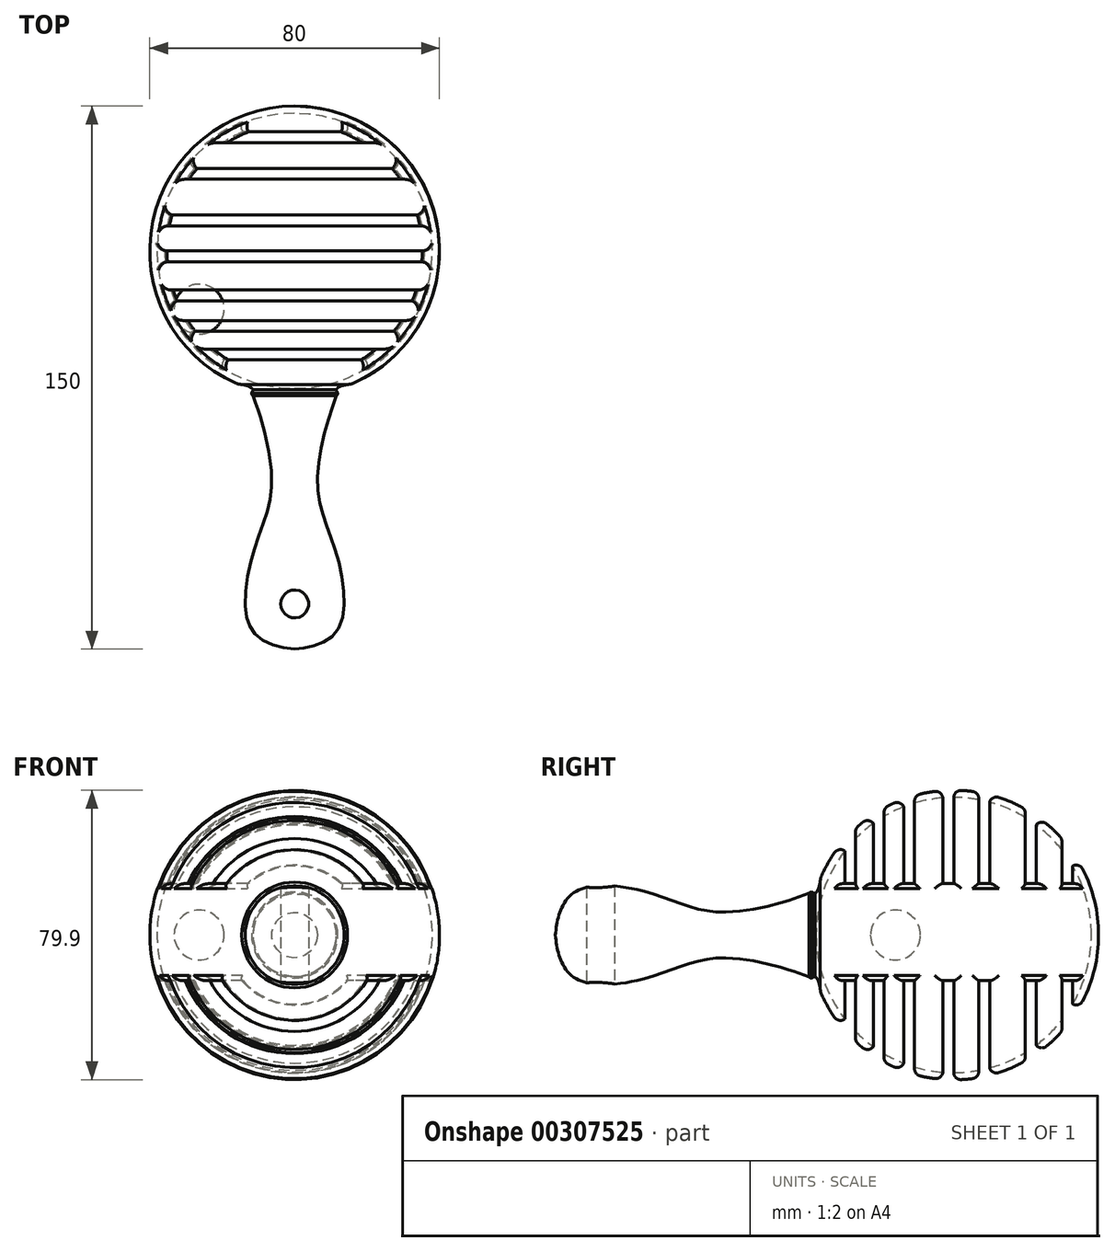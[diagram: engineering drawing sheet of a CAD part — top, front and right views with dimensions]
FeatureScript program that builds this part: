
annotation { "Feature Type Name" : "Feature", "Feature Type Description" : "" }
export const myFeature = defineFeature(function(context is Context, id is Id, definition is map)
    precondition{}
    {
        {
            var Q0;
            Q0=qCreatedBy(makeId("Top.planeOp"),FACE);
            var sketch = newSketch(context, id + "F0", { "sketchPlane" : qUnion([Q0])});
            skArc(sketch, "E0", {"start": v(11.53, -38.3) * mm, "mid": v(39.57, 5.83) * mm, "end": v(0, 40) * mm});
            skArc(sketch, "E1", {"start": v(0, -38) * mm, "mid": v(38, 0) * mm, "end": v(0, 38) * mm});
            skLineSegment(sketch, "E2", {"start": v(0, 40) * mm, "end": v(0, 38) * mm});
            skPoint(sketch, "E3.orphan", {"position": v(0, 47.99) * mm});
            skLineSegment(sketch, "E4.trimOffspring", {"start": v(0, -38) * mm, "end": v(0, -40) * mm});
            skLineSegment(sketch, "E5.bottom", {"start": v(0, -40) * mm, "end": v(11.53, -40) * mm, "construction": true});
            skLineSegment(sketch, "E5.top", {"start": v(0, -110) * mm, "end": v(11.53, -110) * mm, "construction": true});
            skLineSegment(sketch, "E5.left", {"start": v(0, -40) * mm, "end": v(0, -110) * mm, "construction": true});
            skLineSegment(sketch, "E5.right", {"start": v(11.53, -40) * mm, "end": v(11.53, -110) * mm, "construction": true});
            skFitSpline(sketch, "E6", {"points": [v(11.53, -40) * mm, v(6.31, -64.44) * mm, v(11.53, -83.61) * mm, v(11.53, -105.15) * mm, v(0, -110) * mm], "startDerivative": vector(-24.57, -62.37) * mm, "endDerivative": vector(-51.62, -4) * mm});
            skLineSegment(sketch, "E7", {"start": v(0, -110) * mm, "end": v(0, -38) * mm});
            skFitSpline(sketch, "E8", {"points": [v(11.53, -40) * mm, v(11.53, -38.3) * mm, v(15.84, -36.73) * mm, v(13.87, -37.35) * mm], "startDerivative": vector(9.54, 10.18) * mm, "endDerivative": vector(-21.06, -2.87) * mm});
            skFitSpline(sketch, "E9", {"points": [v(11.53, -40) * mm, v(11.53, -38.3) * mm, v(15.3, -37.1) * mm, v(14.9, -38.3) * mm], "startDerivative": vector(8.59, 7.83) * mm, "endDerivative": vector(-7.06, -1.53) * mm});
            skSolve(sketch);
        }
        {
            var Q0;
            {var subQ1=sQuery(id+"F0.wireOp",EDGE,"E1");Q0=makeQuery(id+"F0.imprint","IMPRINT",FACE,{"disambiguationData":[TD([[makeQuery(id+"F0.imprint","IMPRINT",EDGE,{"derivedFrom":subQ1}),-1.0]])]});}
            var Q1;
            Q1=sQuery(id+"F0.wireOp",EDGE,"E7");
            revolve(context, id + "F1", {"entities" : qUnion([Q0]), "axis" : qUnion([Q1]), "revolveType" : RevolveType.FULL});
        }
        {
            var Q0;
            Q0=qCreatedBy(makeId("Right.planeOp"),FACE);
            var sketch = newSketch(context, id + "F2", { "sketchPlane" : qUnion([Q0])});
            skLineSegment(sketch, "E10.bottom", {"start": v(-30.1, 14.18) * mm, "end": v(-27.1, 14.18) * mm});
            skLineSegment(sketch, "E11.bottom", {"start": v(-30.1, 48.04) * mm, "end": v(-27.1, 48.04) * mm});
            skLineSegment(sketch, "E11.top", {"start": v(-30.1, -43.05) * mm, "end": v(-27.1, -43.05) * mm});
            skLineSegment(sketch, "E11.left", {"start": v(-30.1, 48.04) * mm, "end": v(-30.1, 14.18) * mm});
            skLineSegment(sketch, "E11.right", {"start": v(-27.1, 48.04) * mm, "end": v(-27.1, 14.18) * mm});
            skLineSegment(sketch, "E12.bottom", {"start": v(-22.22, 48.3) * mm, "end": v(-19.22, 48.3) * mm});
            skLineSegment(sketch, "E12.top", {"start": v(-22.22, -43.31) * mm, "end": v(-19.22, -43.31) * mm});
            skLineSegment(sketch, "E12.left", {"start": v(-22.22, 48.3) * mm, "end": v(-22.22, 14.18) * mm});
            skLineSegment(sketch, "E12.right", {"start": v(-19.22, 48.3) * mm, "end": v(-19.22, 14.18) * mm});
            skLineSegment(sketch, "E13.bottom", {"start": v(-13.82, 48.04) * mm, "end": v(-10.82, 48.04) * mm});
            skLineSegment(sketch, "E13.top", {"start": v(-13.82, -46.73) * mm, "end": v(-10.82, -46.73) * mm});
            skLineSegment(sketch, "E13.left", {"start": v(-13.82, 48.04) * mm, "end": v(-13.82, 14.18) * mm});
            skLineSegment(sketch, "E13.right", {"start": v(-10.82, 48.04) * mm, "end": v(-10.82, 14.18) * mm});
            skLineSegment(sketch, "E14.bottom", {"start": v(-3, 49.61) * mm, "end": v(0, 49.61) * mm});
            skLineSegment(sketch, "E14.top", {"start": v(-3, -50.66) * mm, "end": v(0, -50.66) * mm});
            skLineSegment(sketch, "E14.left", {"start": v(-3, 49.61) * mm, "end": v(-3, 14.18) * mm});
            skLineSegment(sketch, "E14.right", {"start": v(0, 49.61) * mm, "end": v(0, 14.18) * mm});
            skPoint(sketch, "E15.firstSnap0", {"position": v(6.92, 14.18) * mm});
            skLineSegment(sketch, "E15.bottom", {"start": v(6.92, 48.83) * mm, "end": v(9.92, 48.83) * mm});
            skLineSegment(sketch, "E15.top", {"start": v(6.92, -54.34) * mm, "end": v(9.92, -54.34) * mm});
            skLineSegment(sketch, "E15.left", {"start": v(6.92, 48.83) * mm, "end": v(6.92, 14.18) * mm});
            skLineSegment(sketch, "E15.right", {"start": v(9.92, 48.83) * mm, "end": v(9.92, 14.18) * mm});
            skLineSegment(sketch, "E16.bottom", {"start": v(19.78, 48.83) * mm, "end": v(22.78, 48.83) * mm});
            skLineSegment(sketch, "E16.top", {"start": v(19.78, -47.78) * mm, "end": v(22.78, -47.78) * mm});
            skLineSegment(sketch, "E16.left", {"start": v(19.78, 48.83) * mm, "end": v(19.78, 14.18) * mm});
            skLineSegment(sketch, "E16.right", {"start": v(22.78, 48.83) * mm, "end": v(22.78, 14.18) * mm});
            skLineSegment(sketch, "E17.bottom", {"start": v(29.87, 48.3) * mm, "end": v(32.87, 48.3) * mm});
            skLineSegment(sketch, "E17.top", {"start": v(29.87, -47.78) * mm, "end": v(32.87, -47.78) * mm});
            skLineSegment(sketch, "E17.left", {"start": v(29.87, 48.3) * mm, "end": v(29.87, 14.18) * mm});
            skLineSegment(sketch, "E17.right", {"start": v(32.87, 48.3) * mm, "end": v(32.87, 14.18) * mm});
            skPoint(sketch, "E18.orphan", {"position": v(46.3, 14.18) * mm});
            skLineSegment(sketch, "E19.trimOffspring", {"start": v(29.87, 14.18) * mm, "end": v(32.87, 14.18) * mm});
            skLineSegment(sketch, "E20.trimOffspring", {"start": v(29.87, -12.6) * mm, "end": v(29.87, -47.78) * mm});
            skLineSegment(sketch, "E21.trimOffspring", {"start": v(32.87, -12.6) * mm, "end": v(32.87, -47.78) * mm});
            skLineSegment(sketch, "E22.trimOffspring", {"start": v(22.78, -12.6) * mm, "end": v(22.78, -47.78) * mm});
            skLineSegment(sketch, "E23.trimOffspring", {"start": v(19.78, -12.6) * mm, "end": v(19.78, -47.78) * mm});
            skLineSegment(sketch, "E24.trimOffspring", {"start": v(9.92, -12.6) * mm, "end": v(9.92, -54.34) * mm});
            skLineSegment(sketch, "E25.trimOffspring", {"start": v(6.92, -12.6) * mm, "end": v(6.92, -54.34) * mm});
            skLineSegment(sketch, "E26.trimOffspring", {"start": v(0, -12.6) * mm, "end": v(0, -50.66) * mm});
            skLineSegment(sketch, "E27.trimOffspring", {"start": v(-3, -12.6) * mm, "end": v(-3, -50.66) * mm});
            skLineSegment(sketch, "E28.trimOffspring", {"start": v(-10.82, -12.6) * mm, "end": v(-10.82, -46.73) * mm});
            skLineSegment(sketch, "E29.trimOffspring", {"start": v(-13.82, -12.6) * mm, "end": v(-13.82, -46.73) * mm});
            skLineSegment(sketch, "E30.trimOffspring", {"start": v(-19.22, -12.6) * mm, "end": v(-19.22, -43.31) * mm});
            skLineSegment(sketch, "E31.trimOffspring", {"start": v(-22.22, -12.6) * mm, "end": v(-22.22, -43.31) * mm});
            skLineSegment(sketch, "E32.trimOffspring", {"start": v(-27.1, -12.6) * mm, "end": v(-27.1, -43.05) * mm});
            skLineSegment(sketch, "E33.trimOffspring", {"start": v(-30.1, -12.6) * mm, "end": v(-30.1, -43.05) * mm});
            skLineSegment(sketch, "E34.trimOffspring", {"start": v(-22.22, 14.18) * mm, "end": v(-19.22, 14.18) * mm});
            skPoint(sketch, "E35.orphan", {"position": v(-32.46, 14.18) * mm});
            skLineSegment(sketch, "E36.trimOffspring", {"start": v(-13.82, 14.18) * mm, "end": v(-10.82, 14.18) * mm});
            skLineSegment(sketch, "E37", {"start": v(-3, 14.18) * mm, "end": v(0, 14.18) * mm});
            skLineSegment(sketch, "E38", {"start": v(6.92, 14.18) * mm, "end": v(9.92, 14.18) * mm});
            skLineSegment(sketch, "E39", {"start": v(19.78, 14.18) * mm, "end": v(22.78, 14.18) * mm});
            skLineSegment(sketch, "E40", {"start": v(-30.1, -12.6) * mm, "end": v(-27.1, -12.6) * mm});
            skLineSegment(sketch, "E41", {"start": v(-22.22, -12.6) * mm, "end": v(-19.22, -12.6) * mm});
            skLineSegment(sketch, "E42", {"start": v(-13.82, -12.6) * mm, "end": v(-10.82, -12.6) * mm});
            skLineSegment(sketch, "E43", {"start": v(-3, -12.6) * mm, "end": v(0, -12.6) * mm});
            skLineSegment(sketch, "E44", {"start": v(6.92, -12.6) * mm, "end": v(9.92, -12.6) * mm});
            skLineSegment(sketch, "E45", {"start": v(19.78, -12.6) * mm, "end": v(22.78, -12.6) * mm});
            skLineSegment(sketch, "E46", {"start": v(29.87, -12.6) * mm, "end": v(32.87, -12.6) * mm});
            skSolve(sketch);
        }
        {
            var Q0;
            Q0 = qSketchRegion(id + "F2", true);
            extrude(context, id + "F3", {"entities" : qUnion([Q0]), "operationType" : NewBodyOperationType.REMOVE, "endBound" : BoundingType.SYMMETRIC, "depth" : 80 * mm});
        }
        {
            var Q0;
            Q0=qCreatedBy(makeId("Top.planeOp"),FACE);
            var sketch = newSketch(context, id + "F4", { "sketchPlane" : qUnion([Q0])});
            skArc(sketch, "E47", {"start": v(-30.11, 10.82) * mm, "mid": v(-37.61, 3.32) * mm, "end": v(-30.11, -4.18) * mm});
            skLineSegment(sketch, "E48", {"start": v(-30.11, -4.18) * mm, "end": v(-30.11, 10.82) * mm});
            skArc(sketch, "E49", {"start": v(-26.4, -9.18) * mm, "mid": v(-33.3, -16.09) * mm, "end": v(-26.4, -23) * mm});
            skLineSegment(sketch, "E50", {"start": v(-26.4, -16.09) * mm, "end": v(-26.4, -23) * mm});
            skLineSegment(sketch, "E51", {"start": v(-26.4, -16.09) * mm, "end": v(-26.4, -9.18) * mm});
            skSolve(sketch);
        }
        {
            var Q0;
            Q0=makeQuery(id+"F4.imprint","IMPRINT",FACE,{"disambiguationData":[TD([[makeQuery(id+"F4.imprint","IMPRINT",EDGE,{"derivedFrom":sQuery(id+"F4.wireOp",EDGE,"E49")}),1.0]])]});
            var Q1;
            Q1=sQuery(id+"F4.wireOp",EDGE,"E51");
            revolve(context, id + "F5", {"entities" : qUnion([Q0]), "axis" : qUnion([Q1]), "revolveType" : RevolveType.FULL});
        }
        {
            var Q0;
            Q0=sQuery(id+"F4.wireOp",EDGE,"E47");
            var Q1;
            Q1=sQuery(id+"F4.wireOp",EDGE,"E48");
            revolve(context, id + "F6", {"bodyType" : ToolBodyType.SURFACE, "surfaceEntities" : qUnion([Q0]), "axis" : qUnion([Q1]), "revolveType" : RevolveType.FULL});
        }
        {
            var Q0;
            Q0=qCreatedBy(makeId("Top.planeOp"),FACE);
            var sketch = newSketch(context, id + "F7", { "sketchPlane" : qUnion([Q0])});
            skCircle(sketch, "E52", {"center": v(0, -97.5) * mm, "radius": 3.86 * mm});
            skSolve(sketch);
        }
        {
            var Q0;
            Q0 = qSketchRegion(id + "F7", true);
            var Q1;
            Q1=sQuery(id+"F7.wireOp",EDGE,"E52");
            extrude(context, id + "F8", {"entities" : qUnion([Q0]), "operationType" : NewBodyOperationType.REMOVE, "surfaceEntities" : qUnion([Q1]), "endBound" : BoundingType.SYMMETRIC, "depth" : 34 * mm});
        }
        {
            var Q0;
            Q0=makeQuery(id+"F3.boolean.opBoolean","INTERSECT",EDGE,{"disambiguationData":[OD(1.0)],"derivedFrom":[makeQuery(id+"F1.opRevolve","SWEPT_FACE",FACE,{"disambiguationData":[OSD([sQuery(id+"F0.wireOp",EDGE,"E0")])]}),makeQuery(id+"F3.opExtrude","SWEPT_FACE",FACE,{"disambiguationData":[OSD([sQuery(id+"F2.wireOp",EDGE,"E39")])]})]});
            var Q1;
            Q1=makeQuery(id+"F3.boolean.opBoolean","INTERSECT",EDGE,{"derivedFrom":[makeQuery(id+"F1.opRevolve","SWEPT_FACE",FACE,{"disambiguationData":[OSD([sQuery(id+"F0.wireOp",EDGE,"E0")])]}),makeQuery(id+"F3.opExtrude","SWEPT_FACE",FACE,{"disambiguationData":[OSD([sQuery(id+"F2.wireOp",EDGE,"E16.right")])]})]});
            var Q2;
            Q2=makeQuery(id+"F3.boolean.opBoolean","INTERSECT",EDGE,{"derivedFrom":[makeQuery(id+"F1.opRevolve","SWEPT_FACE",FACE,{"disambiguationData":[OSD([sQuery(id+"F0.wireOp",EDGE,"E0")])]}),makeQuery(id+"F3.opExtrude","SWEPT_FACE",FACE,{"disambiguationData":[OSD([sQuery(id+"F2.wireOp",EDGE,"E16.left")])]})]});
            var Q3;
            Q3=makeQuery(id+"F3.boolean.opBoolean","INTERSECT",EDGE,{"derivedFrom":[makeQuery(id+"F1.opRevolve","SWEPT_FACE",FACE,{"disambiguationData":[OSD([sQuery(id+"F0.wireOp",EDGE,"E0")])]}),makeQuery(id+"F3.opExtrude","SWEPT_FACE",FACE,{"disambiguationData":[OSD([sQuery(id+"F2.wireOp",EDGE,"E15.right")])]})]});
            var Q4;
            Q4=makeQuery(id+"F3.boolean.opBoolean","INTERSECT",EDGE,{"disambiguationData":[OD(1.0)],"derivedFrom":[makeQuery(id+"F1.opRevolve","SWEPT_FACE",FACE,{"disambiguationData":[OSD([sQuery(id+"F0.wireOp",EDGE,"E0")])]}),makeQuery(id+"F3.opExtrude","SWEPT_FACE",FACE,{"disambiguationData":[OSD([sQuery(id+"F2.wireOp",EDGE,"E38")])]})]});
            var Q5;
            Q5=makeQuery(id+"F3.boolean.opBoolean","INTERSECT",EDGE,{"derivedFrom":[makeQuery(id+"F1.opRevolve","SWEPT_FACE",FACE,{"disambiguationData":[OSD([sQuery(id+"F0.wireOp",EDGE,"E0")])]}),makeQuery(id+"F3.opExtrude","SWEPT_FACE",FACE,{"disambiguationData":[OSD([sQuery(id+"F2.wireOp",EDGE,"E15.left")])]})]});
            var Q6;
            Q6=makeQuery(id+"F3.boolean.opBoolean","INTERSECT",EDGE,{"derivedFrom":[makeQuery(id+"F1.opRevolve","SWEPT_FACE",FACE,{"disambiguationData":[OSD([sQuery(id+"F0.wireOp",EDGE,"E0")])]}),makeQuery(id+"F3.opExtrude","SWEPT_FACE",FACE,{"disambiguationData":[OSD([sQuery(id+"F2.wireOp",EDGE,"E14.right")])]})]});
            var Q7;
            Q7=makeQuery(id+"F3.boolean.opBoolean","INTERSECT",EDGE,{"derivedFrom":[makeQuery(id+"F1.opRevolve","SWEPT_FACE",FACE,{"disambiguationData":[OSD([sQuery(id+"F0.wireOp",EDGE,"E0")])]}),makeQuery(id+"F3.opExtrude","SWEPT_FACE",FACE,{"disambiguationData":[OSD([sQuery(id+"F2.wireOp",EDGE,"E14.left")])]})]});
            var Q8;
            Q8=makeQuery(id+"F3.boolean.opBoolean","INTERSECT",EDGE,{"disambiguationData":[OD(1.0)],"derivedFrom":[makeQuery(id+"F1.opRevolve","SWEPT_FACE",FACE,{"disambiguationData":[OSD([sQuery(id+"F0.wireOp",EDGE,"E0")])]}),makeQuery(id+"F3.opExtrude","SWEPT_FACE",FACE,{"disambiguationData":[OSD([sQuery(id+"F2.wireOp",EDGE,"E37")])]})]});
            var Q9;
            Q9=makeQuery(id+"F3.boolean.opBoolean","INTERSECT",EDGE,{"disambiguationData":[OD(1.0)],"derivedFrom":[makeQuery(id+"F1.opRevolve","SWEPT_FACE",FACE,{"disambiguationData":[OSD([sQuery(id+"F0.wireOp",EDGE,"E0")])]}),makeQuery(id+"F3.opExtrude","SWEPT_FACE",FACE,{"disambiguationData":[OSD([sQuery(id+"F2.wireOp",EDGE,"E36.trimOffspring")])]})]});
            var Q10;
            Q10=makeQuery(id+"F3.boolean.opBoolean","INTERSECT",EDGE,{"derivedFrom":[makeQuery(id+"F1.opRevolve","SWEPT_FACE",FACE,{"disambiguationData":[OSD([sQuery(id+"F0.wireOp",EDGE,"E0")])]}),makeQuery(id+"F3.opExtrude","SWEPT_FACE",FACE,{"disambiguationData":[OSD([sQuery(id+"F2.wireOp",EDGE,"E13.right")])]})]});
            var Q11;
            Q11=makeQuery(id+"F3.boolean.opBoolean","INTERSECT",EDGE,{"derivedFrom":[makeQuery(id+"F1.opRevolve","SWEPT_FACE",FACE,{"disambiguationData":[OSD([sQuery(id+"F0.wireOp",EDGE,"E0")])]}),makeQuery(id+"F3.opExtrude","SWEPT_FACE",FACE,{"disambiguationData":[OSD([sQuery(id+"F2.wireOp",EDGE,"E13.left")])]})]});
            var Q12;
            Q12=makeQuery(id+"F3.boolean.opBoolean","INTERSECT",EDGE,{"derivedFrom":[makeQuery(id+"F1.opRevolve","SWEPT_FACE",FACE,{"disambiguationData":[OSD([sQuery(id+"F0.wireOp",EDGE,"E0")])]}),makeQuery(id+"F3.opExtrude","SWEPT_FACE",FACE,{"disambiguationData":[OSD([sQuery(id+"F2.wireOp",EDGE,"E12.right")])]})]});
            var Q13;
            Q13=makeQuery(id+"F3.boolean.opBoolean","INTERSECT",EDGE,{"disambiguationData":[OD(1.0)],"derivedFrom":[makeQuery(id+"F1.opRevolve","SWEPT_FACE",FACE,{"disambiguationData":[OSD([sQuery(id+"F0.wireOp",EDGE,"E0")])]}),makeQuery(id+"F3.opExtrude","SWEPT_FACE",FACE,{"disambiguationData":[OSD([sQuery(id+"F2.wireOp",EDGE,"E34.trimOffspring")])]})]});
            var Q14;
            Q14=makeQuery(id+"F3.boolean.opBoolean","INTERSECT",EDGE,{"derivedFrom":[makeQuery(id+"F1.opRevolve","SWEPT_FACE",FACE,{"disambiguationData":[OSD([sQuery(id+"F0.wireOp",EDGE,"E0")])]}),makeQuery(id+"F3.opExtrude","SWEPT_FACE",FACE,{"disambiguationData":[OSD([sQuery(id+"F2.wireOp",EDGE,"E12.left")])]})]});
            var Q15;
            Q15=makeQuery(id+"F3.boolean.opBoolean","INTERSECT",EDGE,{"derivedFrom":[makeQuery(id+"F1.opRevolve","SWEPT_FACE",FACE,{"disambiguationData":[OSD([sQuery(id+"F0.wireOp",EDGE,"E0")])]}),makeQuery(id+"F3.opExtrude","SWEPT_FACE",FACE,{"disambiguationData":[OSD([sQuery(id+"F2.wireOp",EDGE,"E11.left")])]})]});
            var Q16;
            Q16=makeQuery(id+"F3.boolean.opBoolean","INTERSECT",EDGE,{"disambiguationData":[OD(1.0)],"derivedFrom":[makeQuery(id+"F1.opRevolve","SWEPT_FACE",FACE,{"disambiguationData":[OSD([sQuery(id+"F0.wireOp",EDGE,"E0")])]}),makeQuery(id+"F3.opExtrude","SWEPT_FACE",FACE,{"disambiguationData":[OSD([sQuery(id+"F2.wireOp",EDGE,"E10.bottom")])]})]});
            var Q17;
            Q17=makeQuery(id+"F3.boolean.opBoolean","INTERSECT",EDGE,{"derivedFrom":[makeQuery(id+"F1.opRevolve","SWEPT_FACE",FACE,{"disambiguationData":[OSD([sQuery(id+"F0.wireOp",EDGE,"E0")])]}),makeQuery(id+"F3.opExtrude","SWEPT_FACE",FACE,{"disambiguationData":[OSD([sQuery(id+"F2.wireOp",EDGE,"E11.right")])]})]});
            var Q18;
            Q18=makeQuery(id+"F3.boolean.opBoolean","INTERSECT",EDGE,{"derivedFrom":[makeQuery(id+"F1.opRevolve","SWEPT_FACE",FACE,{"disambiguationData":[OSD([sQuery(id+"F0.wireOp",EDGE,"E0")])]}),makeQuery(id+"F3.opExtrude","SWEPT_FACE",FACE,{"disambiguationData":[OSD([sQuery(id+"F2.wireOp",EDGE,"E17.left")])]})]});
            var Q19;
            Q19=makeQuery(id+"F3.boolean.opBoolean","INTERSECT",EDGE,{"disambiguationData":[OD(1.0)],"derivedFrom":[makeQuery(id+"F1.opRevolve","SWEPT_FACE",FACE,{"disambiguationData":[OSD([sQuery(id+"F0.wireOp",EDGE,"E0")])]}),makeQuery(id+"F3.opExtrude","SWEPT_FACE",FACE,{"disambiguationData":[OSD([sQuery(id+"F2.wireOp",EDGE,"E19.trimOffspring")])]})]});
            var Q20;
            Q20=makeQuery(id+"F3.boolean.opBoolean","INTERSECT",EDGE,{"derivedFrom":[makeQuery(id+"F1.opRevolve","SWEPT_FACE",FACE,{"disambiguationData":[OSD([sQuery(id+"F0.wireOp",EDGE,"E0")])]}),makeQuery(id+"F3.opExtrude","SWEPT_FACE",FACE,{"disambiguationData":[OSD([sQuery(id+"F2.wireOp",EDGE,"E17.right")])]})]});
            var Q21;
            Q21=makeQuery(id+"F1.opRevolve","SWEPT_FACE",FACE,{"disambiguationData":[OSD([sQuery(id+"F0.wireOp",EDGE,"E0")])]});
            var Q22;
            Q22=makeQuery(id+"F3.boolean.opBoolean","INTERSECT",EDGE,{"disambiguationData":[OD(0.0)],"derivedFrom":[makeQuery(id+"F1.opRevolve","SWEPT_FACE",FACE,{"disambiguationData":[OSD([sQuery(id+"F0.wireOp",EDGE,"E0")])]}),makeQuery(id+"F3.opExtrude","SWEPT_FACE",FACE,{"disambiguationData":[OSD([sQuery(id+"F2.wireOp",EDGE,"E10.bottom")])]})]});
            var Q23;
            Q23=makeQuery(id+"F3.boolean.opBoolean","INTERSECT",EDGE,{"disambiguationData":[OD(0.0)],"derivedFrom":[makeQuery(id+"F1.opRevolve","SWEPT_FACE",FACE,{"disambiguationData":[OSD([sQuery(id+"F0.wireOp",EDGE,"E0")])]}),makeQuery(id+"F3.opExtrude","SWEPT_FACE",FACE,{"disambiguationData":[OSD([sQuery(id+"F2.wireOp",EDGE,"E34.trimOffspring")])]})]});
            var Q24;
            Q24=makeQuery(id+"F3.boolean.opBoolean","INTERSECT",EDGE,{"disambiguationData":[OD(0.0)],"derivedFrom":[makeQuery(id+"F1.opRevolve","SWEPT_FACE",FACE,{"disambiguationData":[OSD([sQuery(id+"F0.wireOp",EDGE,"E0")])]}),makeQuery(id+"F3.opExtrude","SWEPT_FACE",FACE,{"disambiguationData":[OSD([sQuery(id+"F2.wireOp",EDGE,"E36.trimOffspring")])]})]});
            var Q25;
            Q25=makeQuery(id+"F3.boolean.opBoolean","INTERSECT",EDGE,{"disambiguationData":[OD(0.0)],"derivedFrom":[makeQuery(id+"F1.opRevolve","SWEPT_FACE",FACE,{"disambiguationData":[OSD([sQuery(id+"F0.wireOp",EDGE,"E0")])]}),makeQuery(id+"F3.opExtrude","SWEPT_FACE",FACE,{"disambiguationData":[OSD([sQuery(id+"F2.wireOp",EDGE,"E37")])]})]});
            var Q26;
            Q26=makeQuery(id+"F3.boolean.opBoolean","INTERSECT",EDGE,{"disambiguationData":[OD(0.0)],"derivedFrom":[makeQuery(id+"F1.opRevolve","SWEPT_FACE",FACE,{"disambiguationData":[OSD([sQuery(id+"F0.wireOp",EDGE,"E0")])]}),makeQuery(id+"F3.opExtrude","SWEPT_FACE",FACE,{"disambiguationData":[OSD([sQuery(id+"F2.wireOp",EDGE,"E38")])]})]});
            var Q27;
            Q27=makeQuery(id+"F3.boolean.opBoolean","INTERSECT",EDGE,{"disambiguationData":[OD(0.0)],"derivedFrom":[makeQuery(id+"F1.opRevolve","SWEPT_FACE",FACE,{"disambiguationData":[OSD([sQuery(id+"F0.wireOp",EDGE,"E0")])]}),makeQuery(id+"F3.opExtrude","SWEPT_FACE",FACE,{"disambiguationData":[OSD([sQuery(id+"F2.wireOp",EDGE,"E39")])]})]});
            var Q28;
            Q28=makeQuery(id+"F3.boolean.opBoolean","INTERSECT",EDGE,{"disambiguationData":[OD(0.0)],"derivedFrom":[makeQuery(id+"F1.opRevolve","SWEPT_FACE",FACE,{"disambiguationData":[OSD([sQuery(id+"F0.wireOp",EDGE,"E0")])]}),makeQuery(id+"F3.opExtrude","SWEPT_FACE",FACE,{"disambiguationData":[OSD([sQuery(id+"F2.wireOp",EDGE,"E19.trimOffspring")])]})]});
            fillet(context, id + "F9", {"entities" : qUnion([Q0, Q1, Q2, Q3, Q4, Q5, Q6, Q7, Q8, Q9, Q10, Q11, Q12, Q13, Q14, Q15, Q16, Q17, Q18, Q19, Q20, Q21, Q22, Q23, Q24, Q25, Q26, Q27, Q28]), "radius" : 2 * mm, "tangentPropagation" : true, "allowEdgeOverflow" : false});
        }
    });
